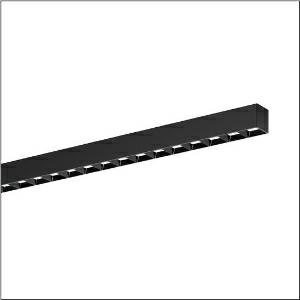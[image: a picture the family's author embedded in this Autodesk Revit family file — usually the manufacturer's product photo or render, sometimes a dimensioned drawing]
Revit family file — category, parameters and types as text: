
# Revit family: silica_r__21_51mx22tctab_4aec
name_source: partatom
category: Lighting Fixtures
units: mm (PartAtom-declared; Revit-internal decimal feet)

## family parameters
Cut with Voids When Loaded = No
Host = Face
Light Source = No
Part Type = Normal
Room Calculation Point = No
Round Connector Dimension = Use Diameter
Shared = No

## types (1)
- --- (1 x LED, 9300 lm, 80.4 W, 6500K)
    Apparent Load = 80 VA
    CIE Flux Codes = 84 100 100 100 100
    Color Rendering = 80
    Color Temperature = 6500K
    Default Elevation = 1800 mm
    Description = Silica® 21, office luminaire, primary light control with darklight reflector, of PMMA, black, CAT 2 (L<= 3000cd/m²), light emission: direct distribution, primary light characteristic: symmetric, installation type: surface-mounted, LED, rated luminous flux: 9.300lm, luminous efficacy: 110lm/W, light colour: 8tw, colour temperature: 2700..6500K, control gear: DALI DT8, with terminal, 3+2-pole, max. 2.5mm², mains connection: 220..240V, AC, 50/60Hz, rated input power: 84.5W, luminaire housing, of aluminium, matt jet black (RAL 9005), length: 3.004mm, width: 53mm, height: 53mm, protection rating (complete): IP20, insulation class (complete): insulation class I (protective earthing), certification: CE, permissible operating ambient temperature: 0..+35°C, standard: EN 50419, packaging unit: 1 piece
    Height = 53 mm
    Lamp = 1 x LED
    Lamp Light Flux = 9300 lm
    Lamp Power = 80.4 W
    Lamp count = 1
    Length = 3004 mm
    Luminous efficacy = 116 lm/W
    Manufacturer = Siteco
    ModVariant = No
    Model = 51MX22TCTAB
    Mounting Place = Ceiling
    Mounting Type = Surface mounted
    Number of Poles = 1
    OnlyDefault = Yes
    Power Factor = 1
    Product Name = Silica® 21
    Product group = office luminaire | ceiling mounted
    ProductGroupID = 302
    Protection Class = Protection class I
    Protection Degree = IP 20
    RLX_Detail_Level = 1
    RLX_Emergency_Light_Flux = 0 lm
    RLX_Emergency_Type = 0
    RLX_Emergency_Type_DB = No
    RlxData = <blob elided: 61409 chars, md5=f921a0e3>
    Socket = socket
    Standby Power = 0 W
    System Light Flux = 9300 lm
    System Power = 80 W
    Type Comments = individual setting
    Type Image = l_1335908.jpg
    URL = http://relux.com
    VarID = @adj_140130
    Voltage = 0 V
    Weight = 0.00 kg
    Width = 53 mm

## geometry (parser evidence)
native form markers: Blend x4, Sweep x13
no freeform markers — native parametric forms only
